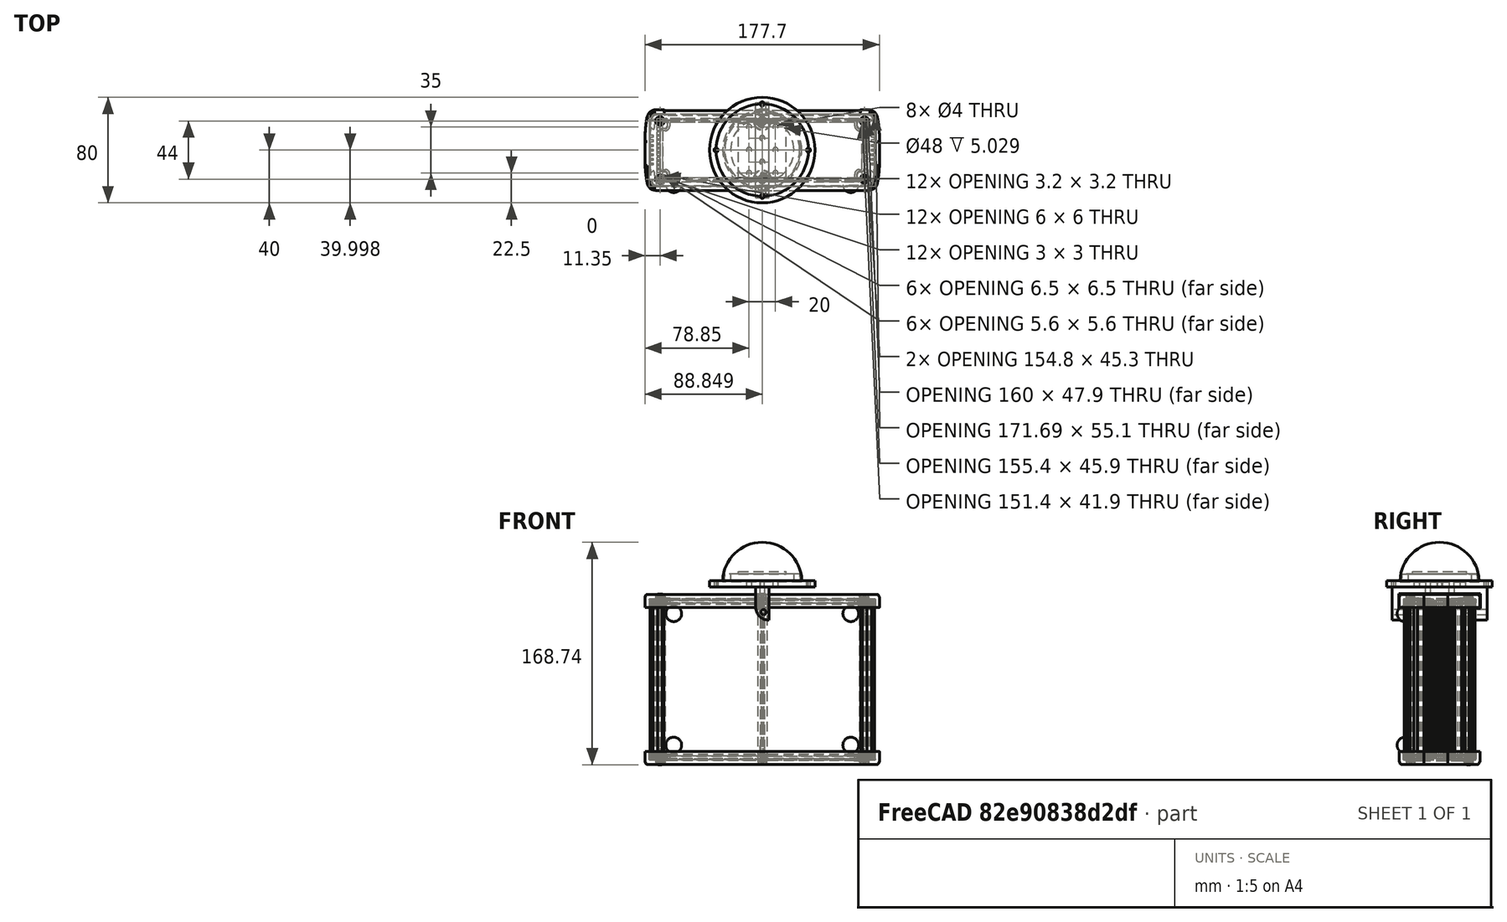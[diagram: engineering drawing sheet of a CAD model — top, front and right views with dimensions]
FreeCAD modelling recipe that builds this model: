
FCSTD DOCUMENT  (FreeCAD 0.20R29177 (Git))
Label: lightModule2022_07_18
License: All rights reserved
LicenseURL: http://en.wikipedia.org/wiki/All_rights_reserved
objects: Part::Cylinder×21, Part::MultiFuse×12, Part::Cut×6, Part::Box×5, Part::Sphere×2, Part::Feature×1, Part::MultiCommon×1
note: 48 computed .brp shape members not serialized (recipe doc carries the construction recipe); baked Part::Feature solids carry a one-line shape summary decoded from their .brp

FEATURE [Part::Box] Box  label="out"
  AttacherType = Attacher::AttachEngine3D
  Height = 25
  Length = 10
  Placement = pos=(0,-36,45) rot=(0,0,1;0rad)
  Width = 72
FEATURE [Part::Box] Box001  label="in"
  AttacherType = Attacher::AttachEngine3D
  Height = 11
  Length = 10
  Placement = pos=(0,-31,54) rot=(0,0,1;0rad)
  Width = 62
FEATURE [Part::Box] Box002  label="in001"
  AttacherType = Attacher::AttachEngine3D
  Height = 11
  Length = 10
  Placement = pos=(0,-27,45) rot=(0,0,1;0rad)
  Width = 54
FEATURE [Part::Cylinder] Cylinder
  Angle = 90
  AttacherType = Attacher::AttachEngine3D
  FirstAngle = 0
  Height = 5
  Placement = pos=(10,31,55) rot=(0.57735,-0.57735,-0.57735;4.18879rad)
  Radius = 10
  SecondAngle = 0
FEATURE [Part::Cylinder] Cylinder001
  Angle = 90
  AttacherType = Attacher::AttachEngine3D
  FirstAngle = 0
  Height = 5
  Placement = pos=(10,-31,55) rot=(0,0.707107,-0.707107;3.14159rad)
  Radius = 10
  SecondAngle = 0
FEATURE [Part::MultiFuse] Fusion  label="in002"
  Shapes = -> [Box001,Box002]
FEATURE [Part::Cut] Cut
  Base = -> Box
  Tool = -> Fusion
FEATURE [Part::MultiFuse] Fusion001  label="out001"
  Shapes = -> [Cylinder,Cylinder001,Cut]
FEATURE [Part::Feature] Feature  label="EX-64-002"
  Placement = pos=(5,0,0) rot=(0,0,1;0rad)
  shape: bbox 178.8 x 63.35 x 129.6 mm, 1628 faces, 33 solids (baked)
FEATURE [Part::Cylinder] Cylinder016  label="m3HeastSetCut"
  Angle = 360
  AttacherType = Attacher::AttachEngine3D
  FirstAngle = 0
  Height = 94
  Placement = pos=(6,-47.35,51) rot=(-1,0,0;1.5708rad)
  Radius = 2
  SecondAngle = 0
FEATURE [Part::Box] Box004  label="include"
  AttacherType = Attacher::AttachEngine3D
  Height = 15
  Length = 25
  Placement = pos=(-15,-36,55) rot=(0,0,1;0rad)
  Width = 72
FEATURE [Part::Cylinder] Cylinder017  label="include001"
  Angle = 90
  AttacherType = Attacher::AttachEngine3D
  FirstAngle = 0
  Height = 87
  Placement = pos=(10,-40.75,55) rot=(0.57735,-0.57735,-0.57735;4.18879rad)
  Radius = 10
  SecondAngle = 0
FEATURE [Part::Sphere] Sphere
  Angle1 = 0
  Angle2 = 90
  Angle3 = 360
  AttacherType = Attacher::AttachEngine3D
  Placement = pos=(5,0,74) rot=(0,0,1;0rad)
  Radius = 30
FEATURE [Part::Box] Box005  label="as7265x"
  AttacherType = Attacher::AttachEngine3D
  Height = 2
  Length = 36
  Placement = pos=(-13,-20.5,80) rot=(0,0,1;0rad)
  Width = 41
FEATURE [Part::Cylinder] Cylinder019
  Angle = 360
  AttacherType = Attacher::AttachEngine3D
  FirstAngle = 0
  Height = 10
  Placement = pos=(0,-21,0) rot=(0,0,1;0rad)
  Radius = 2
  SecondAngle = 0
FEATURE [Part::Cylinder] Cylinder020
  Angle = 360
  AttacherType = Attacher::AttachEngine3D
  FirstAngle = 0
  Height = 10
  Placement = pos=(20,-21,0) rot=(0,0,1;0rad)
  Radius = 2
  SecondAngle = 0
FEATURE [Part::MultiFuse] Fusion005  label="m3HeatSetCuts"
  Placement = pos=(-5,38.5,70) rot=(0,0,1;0rad)
  Shapes = -> [Cylinder020,Cylinder019]
FEATURE [Part::Cylinder] Cylinder021
  Angle = 360
  AttacherType = Attacher::AttachEngine3D
  FirstAngle = 0
  Height = 10
  Placement = pos=(0,-21,0) rot=(0,0,1;0rad)
  Radius = 2
  SecondAngle = 0
FEATURE [Part::Cylinder] Cylinder022
  Angle = 360
  AttacherType = Attacher::AttachEngine3D
  FirstAngle = 0
  Height = 10
  Placement = pos=(20,-21,0) rot=(0,0,1;0rad)
  Radius = 2
  SecondAngle = 0
FEATURE [Part::MultiFuse] Fusion006  label="m3HeatSetCuts001"
  Placement = pos=(-5,3.5,70) rot=(0,0,1;0rad)
  Shapes = -> [Cylinder022,Cylinder021]
FEATURE [Part::Cylinder] Cylinder023  label="base"
  Angle = 360
  AttacherType = Attacher::AttachEngine3D
  FirstAngle = 0
  Height = 5
  Placement = pos=(5,0,70) rot=(0,0,1;0rad)
  Radius = 40
  SecondAngle = 0
FEATURE [Part::Sphere] Sphere001  label="SphereBase"
  Angle1 = 0
  Angle2 = 12
  Angle3 = 360
  AttacherType = Attacher::AttachEngine3D
  Placement = pos=(5,0,74) rot=(0,0,1;0rad)
  Radius = 29
FEATURE [Part::Cylinder] Cylinder024  label="baseCut"
  Angle = 360
  AttacherType = Attacher::AttachEngine3D
  FirstAngle = 0
  Height = 7
  Placement = pos=(5,0,74) rot=(0,0,1;0rad)
  Radius = 24
  SecondAngle = 0
FEATURE [Part::Cut] Cut001
  Base = -> Sphere001
  Tool = -> Cylinder024
FEATURE [Part::MultiFuse] Fusion007  label="m3HeatSetCuts002"
  Shapes = -> [Fusion006,Fusion005]
FEATURE [Part::Cylinder] Cylinder025  label="wireCUt"
  Angle = 360
  AttacherType = Attacher::AttachEngine3D
  FirstAngle = 0
  Height = 10
  Placement = pos=(-5,0,70) rot=(0,0,1;0rad)
  Radius = 2
  SecondAngle = 0
FEATURE [Part::Cylinder] Cylinder026  label="wireCUt001"
  Angle = 360
  AttacherType = Attacher::AttachEngine3D
  FirstAngle = 0
  Height = 10
  Placement = pos=(15,0,70) rot=(0,0,1;0rad)
  Radius = 2
  SecondAngle = 0
FEATURE [Part::MultiFuse] Fusion008  label="wireCuts"
  Shapes = -> [Cylinder025,Cylinder026]
FEATURE [Part::Cylinder] Cylinder027  label="m3Cuts"
  Angle = 360
  AttacherType = Attacher::AttachEngine3D
  FirstAngle = 0
  Height = 10
  Placement = pos=(5,-9,70) rot=(0,0,1;0rad)
  Radius = 1.75
  SecondAngle = 0
FEATURE [Part::Cylinder] Cylinder028  label="m3Cuts001"
  Angle = 360
  AttacherType = Attacher::AttachEngine3D
  FirstAngle = 0
  Height = 10
  Placement = pos=(5,9,70) rot=(0,0,1;0rad)
  Radius = 1.75
  SecondAngle = 0
FEATURE [Part::MultiFuse] Fusion009  label="m3Cute"
  Shapes = -> [Cylinder027,Cylinder028]
FEATURE [Part::MultiFuse] Fusion010  label="baseCUts"
  Shapes = -> [Fusion007,Fusion008,Fusion009]
FEATURE [Part::MultiFuse] Fusion011  label="base001"
  Shapes = -> [Cylinder023,Cut001]
FEATURE [Part::Cut] Cut002
  Base = -> Fusion011
  Tool = -> Fusion010
FEATURE [Part::Cylinder] Cylinder029  label="m3Cuts002"
  Angle = 360
  AttacherType = Attacher::AttachEngine3D
  FirstAngle = 0
  Height = 10
  Placement = pos=(5,-9,70) rot=(0,0,1;0rad)
  Radius = 2
  SecondAngle = 0
FEATURE [Part::Cylinder] Cylinder030  label="m3Cuts003"
  Angle = 360
  AttacherType = Attacher::AttachEngine3D
  FirstAngle = 0
  Height = 10
  Placement = pos=(5,9,70) rot=(0,0,1;0rad)
  Radius = 2
  SecondAngle = 0
FEATURE [Part::MultiFuse] Fusion012  label="m3Cute001"
  Placement = pos=(0,0,-5) rot=(0,0,1;0rad)
  Shapes = -> [Cylinder029,Cylinder030]
FEATURE [Part::Cut] Cut003
  Base = -> Fusion001
  Tool = -> Fusion012
FEATURE [Part::Cut] Cut004  label="lowBase"
  Base = -> Cut003
  Tool = -> Cylinder016
FEATURE [Part::Cylinder] Cylinder031  label="base002"
  Angle = 360
  AttacherType = Attacher::AttachEngine3D
  FirstAngle = 0
  Height = 5
  Placement = pos=(5,0,70) rot=(0,0,1;0rad)
  Radius = 35
  SecondAngle = 0
FEATURE [Part::Cylinder] Cylinder032  label="m2HeatSetInsets"
  Angle = 360
  AttacherType = Attacher::AttachEngine3D
  FirstAngle = 0
  Height = 10
  Placement = pos=(-30,0,65) rot=(0,0,1;0rad)
  Radius = 1.6
  SecondAngle = 0
FEATURE [Part::Cylinder] Cylinder033  label="m2HeatSetInsets001"
  Angle = 360
  AttacherType = Attacher::AttachEngine3D
  FirstAngle = 0
  Height = 10
  Placement = pos=(40,0,65) rot=(0,0,1;0rad)
  Radius = 1.6
  SecondAngle = 0
FEATURE [Part::Cylinder] Cylinder034  label="m2HeatSetInsets002"
  Angle = 360
  AttacherType = Attacher::AttachEngine3D
  FirstAngle = 0
  Height = 10
  Placement = pos=(5,35,65) rot=(0,0,1;0rad)
  Radius = 1.6
  SecondAngle = 0
FEATURE [Part::Cylinder] Cylinder035  label="m2HeatSetInsets003"
  Angle = 360
  AttacherType = Attacher::AttachEngine3D
  FirstAngle = 0
  Height = 10
  Placement = pos=(5,-35,65) rot=(0,0,1;0rad)
  Radius = 1.6
  SecondAngle = 0
FEATURE [Part::MultiFuse] Fusion013
  Shapes = -> [Cylinder032,Cylinder033,Cylinder034,Cylinder035]
FEATURE [Part::Cut] Cut005
  Base = -> Cut002
  Tool = -> Fusion013
FEATURE [Part::MultiFuse] Fusion014  label="include002"
  Shapes = -> [Box004,Cylinder017]
FEATURE [Part::MultiCommon] Common
  Shapes = -> [Fusion014,Cut004]
